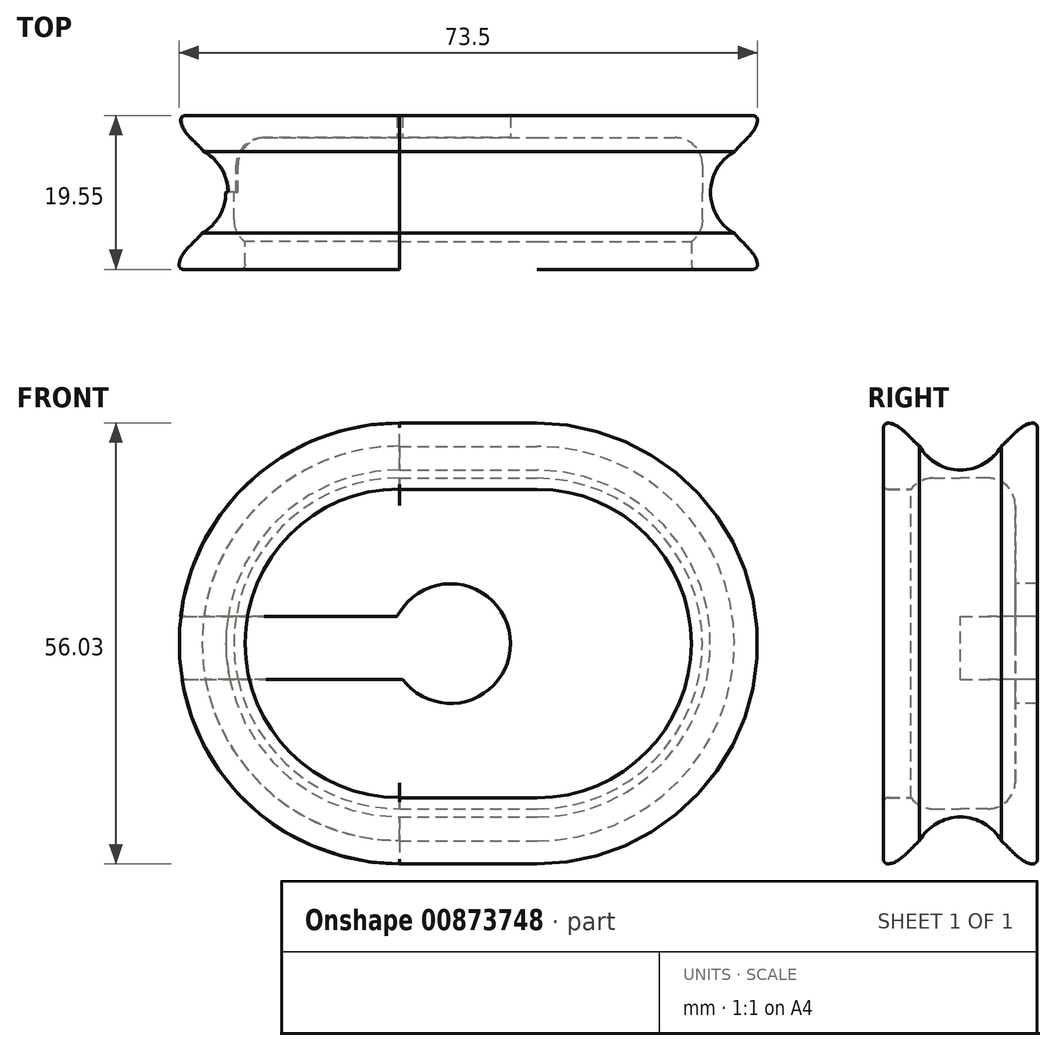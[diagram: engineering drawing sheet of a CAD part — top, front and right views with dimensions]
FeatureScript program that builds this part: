
annotation { "Feature Type Name" : "Feature", "Feature Type Description" : "" }
export const myFeature = defineFeature(function(context is Context, id is Id, definition is map)
    precondition{}
    {
        {
            var Q0;
            Q0=qCreatedBy(makeId("Top.planeOp"),FACE);
            var sketch = newSketch(context, id + "F0", { "sketchPlane" : qUnion([Q0])});
            skLineSegment(sketch, "E0", {"start": v(32.84, -14) * mm, "end": v(32.86, 13.93) * mm, "construction": true});
            skLineSegment(sketch, "E1", {"start": v(39.15, 13.93) * mm, "end": v(0, 13.93) * mm});
            skLineSegment(sketch, "E2", {"start": v(-31.68, 0) * mm, "end": v(51.3, -0.04) * mm, "construction": true});
            skLineSegment(sketch, "E3", {"start": v(26.86, 4.13) * mm, "end": v(26.83, 4.13) * mm, "construction": true});
            skFitSpline(sketch, "E4", {"points": [v(34.01, 4.12) * mm, v(40, 13.93) * mm], "startDerivative": vector(3.62, 13.63) * mm, "endDerivative": vector(-1.34, 11.55) * mm});
            skFitSpline(sketch, "E5.MirrorCS", {"points": [v(34, -4.19) * mm, v(40, -14) * mm], "startDerivative": vector(3.6, -13.63) * mm, "endDerivative": vector(-1.35, -11.55) * mm});
            skLineSegment(sketch, "E6", {"start": v(30.01, 4.92) * mm, "end": v(30.01, -0.03) * mm});
            skLineSegment(sketch, "E7", {"start": v(0, 9.93) * mm, "end": v(0, 13.93) * mm});
            skArc(sketch, "E8.filletArc", {"start": v(30.01, 4.92) * mm, "mid": v(28.55, 8.46) * mm, "end": v(25.01, 9.92) * mm});
            skArc(sketch, "E9.MirrorCS", {"start": v(30, -4.98) * mm, "mid": v(29.47, -7.22) * mm, "end": v(28, -8.99) * mm});
            skLineSegment(sketch, "E10.MirrorCS", {"start": v(30, -4.98) * mm, "end": v(30.01, -0.03) * mm});
            skLineSegment(sketch, "E11", {"start": v(28, -13.13) * mm, "end": v(28, -8.99) * mm});
            skLineSegment(sketch, "E12", {"start": v(0, 3.85) * mm, "end": v(40, 3.83) * mm, "construction": true});
            skLineSegment(sketch, "E13", {"start": v(40, 18.61) * mm, "end": v(40, -32.14) * mm, "construction": true});
            skLineSegment(sketch, "E14", {"start": v(25.01, 9.92) * mm, "end": v(0, 9.93) * mm});
            skLineSegment(sketch, "E15", {"start": v(39.14, -14) * mm, "end": v(28.85, -13.99) * mm});
            skLineSegment(sketch, "E16", {"start": v(36.5, -1.52) * mm, "end": v(36.51, 2.9) * mm, "construction": true});
            skArc(sketch, "E17", {"start": v(35.8, 7.37) * mm, "mid": v(31.48, -0.03) * mm, "end": v(35.8, -7.44) * mm});
            skArc(sketch, "E18.filletArc", {"start": v(39.14, -14) * mm, "mid": v(39.78, -13.7) * mm, "end": v(39.99, -13.02) * mm});
            skArc(sketch, "E19.filletArc", {"start": v(40, 12.95) * mm, "mid": v(39.8, 13.63) * mm, "end": v(39.15, 13.93) * mm});
            skPoint(sketch, "E20.visualSharp", {"position": v(28, -13.99) * mm});
            skArc(sketch, "E20.filletArc", {"start": v(28, -13.13) * mm, "mid": v(28.24, -13.74) * mm, "end": v(28.85, -13.99) * mm});
            skSolve(sketch);
        }
        {
            var Q0;
            Q0=qSketchRegion(id+"F0",true);
            var Q1;
            Q1=qSketchRegion(id+"F0",true);
            var Q2;
            Q2=makeQuery(id+"F0.imprint","IMPRINT",FACE,{"disambiguationData":[TD([[makeQuery(id+"F0.imprint","IMPRINT",EDGE,{"derivedFrom":sQuery(id+"F0.wireOp",EDGE,"E1")}),1.0]])]});
            var Q3;
            Q3=sQuery(id+"F0.wireOp",EDGE,"YOEqnzkB-9UwB-SSfj-woJi-8cwrd5BflBc7");
            var Q4;
            Q4=sQuery(id+"F0.wireOp",EDGE,"E7");
            revolve(context, id + "F1", {"surfaceOperationType" : NewSurfaceOperationType.NEW, "entities" : qUnion([Q0, Q1, Q2]), "axis" : qUnion([Q3, Q4]), "revolveType" : RevolveType.SYMMETRIC, "angle" : 180 * degree});
        }
        {
            var Q0;
            Q0=makeQuery(id+"F1.opRevolve","CAP_FACE",FACE,{"disambiguationData":[OSD([sQuery(id+"F0.wireOp",EDGE,"E1"),sQuery(id+"F0.wireOp",EDGE,"E4"),sQuery(id+"F0.wireOp",EDGE,"pFRlobtz-0q4r-BGyK-Zf5O-oVfqoQiTMujq"),sQuery(id+"F0.wireOp",EDGE,"0d47ac5b-4a7f-461a-a2c7-a7ca7c96fb220.MirrorCS"),sQuery(id+"F0.wireOp",EDGE,"E5.MirrorCS"),sQuery(id+"F0.wireOp",EDGE,"mUEO9S0t-vfNT-DUiq-7ehG-LlwwYBXUM1qr"),sQuery(id+"F0.wireOp",EDGE,"E6"),sQuery(id+"F0.wireOp",EDGE,"E7"),sQuery(id+"F0.wireOp",EDGE,"E8.filletArc"),sQuery(id+"F0.wireOp",EDGE,"E9.MirrorCS"),sQuery(id+"F0.wireOp",EDGE,"E10.MirrorCS"),sQuery(id+"F0.wireOp",EDGE,"DfFPZrzA-9eie-ccyR-lrFW-XJ07qiCjYuLb"),sQuery(id+"F0.wireOp",EDGE,"E11")])],"isStart":false});
            extrude(context, id + "F2", {"entities" : qUnion([Q0]), "operationType" : NewBodyOperationType.ADD, "depth" : 25 * mm, "offsetDistance" : 25 * mm});
        }
        {
            var Q0;
            Q0=makeQuery(id+"F2.opExtrude","CAP_FACE",FACE,{"disambiguationData":[OSD([sQuery(id+"F0.wireOp",EDGE,"E1"),sQuery(id+"F0.wireOp",EDGE,"E4"),sQuery(id+"F0.wireOp",EDGE,"pFRlobtz-0q4r-BGyK-Zf5O-oVfqoQiTMujq"),sQuery(id+"F0.wireOp",EDGE,"0d47ac5b-4a7f-461a-a2c7-a7ca7c96fb220.MirrorCS"),sQuery(id+"F0.wireOp",EDGE,"E5.MirrorCS"),sQuery(id+"F0.wireOp",EDGE,"mUEO9S0t-vfNT-DUiq-7ehG-LlwwYBXUM1qr"),sQuery(id+"F0.wireOp",EDGE,"E6"),sQuery(id+"F0.wireOp",EDGE,"E7"),sQuery(id+"F0.wireOp",EDGE,"E8.filletArc"),sQuery(id+"F0.wireOp",EDGE,"E9.MirrorCS"),sQuery(id+"F0.wireOp",EDGE,"E10.MirrorCS"),sQuery(id+"F0.wireOp",EDGE,"DfFPZrzA-9eie-ccyR-lrFW-XJ07qiCjYuLb"),sQuery(id+"F0.wireOp",EDGE,"E11")])],"isStart":false});
            cPlane(context, id + "F3", {"entities" : qUnion([Q0]), "cplaneType" : CPlaneType.OFFSET, "offset" : 0 * mm, "width" : 150 * mm, "height" : 150 * mm});
        }
        {
            var Q0;
            Q0=qCreatedBy(id+"F3.planeOp",FACE);
            var sketch = newSketch(context, id + "F4", { "sketchPlane" : qUnion([Q0])});
            skLineSegment(sketch, "E21", {"start": v(14, 32.88) * mm, "end": v(-13.93, 32.9) * mm, "construction": true});
            skLineSegment(sketch, "E22", {"start": v(-0.01, -31.64) * mm, "end": v(0.03, 51.34) * mm, "construction": true});
            skLineSegment(sketch, "E23", {"start": v(-4.13, 26.9) * mm, "end": v(-4.13, 26.86) * mm, "construction": true});
            skFitSpline(sketch, "E24", {"points": [v(-4.13, 34.05) * mm, v(-13.93, 40.04) * mm], "startDerivative": vector(-13.63, 3.62) * mm, "endDerivative": vector(-11.55, -1.34) * mm});
            skLineSegment(sketch, "E25", {"start": v(13.22, 0.04) * mm, "end": v(-13.1, 0.04) * mm, "construction": true});
            skFitSpline(sketch, "E26.MirrorCS", {"points": [v(4.19, 34.04) * mm, v(14, 40.03) * mm], "startDerivative": vector(13.63, 3.6) * mm, "endDerivative": vector(11.55, -1.35) * mm});
            skLineSegment(sketch, "E27", {"start": v(-9.93, 0.04) * mm, "end": v(-9.93, 17.9) * mm});
            skLineSegment(sketch, "E28", {"start": v(-4.93, 30.05) * mm, "end": v(0.03, 30.05) * mm});
            skLineSegment(sketch, "E29", {"start": v(-9.93, 0.04) * mm, "end": v(-13.93, 0.04) * mm});
            skPoint(sketch, "E30.visualSharp", {"position": v(-9.93, 22.9) * mm});
            skArc(sketch, "E30.filletArc", {"start": v(-4.93, 30.05) * mm, "mid": v(-8.46, 28.58) * mm, "end": v(-9.93, 25.05) * mm});
            skArc(sketch, "E31.MirrorCS", {"start": v(4.98, 30.04) * mm, "mid": v(7.22, 29.5) * mm, "end": v(8.99, 28.03) * mm});
            skLineSegment(sketch, "E32.MirrorCS", {"start": v(4.98, 30.04) * mm, "end": v(0.03, 30.05) * mm});
            skLineSegment(sketch, "E33", {"start": v(13.13, 28.03) * mm, "end": v(8.99, 28.03) * mm});
            skLineSegment(sketch, "E34", {"start": v(-13.93, 0.04) * mm, "end": v(-13.93, 39.18) * mm});
            skLineSegment(sketch, "E35", {"start": v(13.99, 28.88) * mm, "end": v(14, 39.18) * mm});
            skLineSegment(sketch, "E36", {"start": v(-9.93, 17.9) * mm, "end": v(-9.93, 25.05) * mm});
            skLineSegment(sketch, "E37", {"start": v(-13.93, 40.04) * mm, "end": v(14, 40.03) * mm, "construction": true});
            skArc(sketch, "E38", {"start": v(7.42, 35.82) * mm, "mid": v(0, 31.52) * mm, "end": v(-7.4, 35.85) * mm});
            skPoint(sketch, "E39.visualSharp", {"position": v(13.99, 28.03) * mm});
            skArc(sketch, "E39.filletArc", {"start": v(13.13, 28.03) * mm, "mid": v(13.74, 28.28) * mm, "end": v(13.99, 28.88) * mm});
            skArc(sketch, "E40.filletArc", {"start": v(-12.95, 40.03) * mm, "mid": v(-13.63, 39.83) * mm, "end": v(-13.93, 39.18) * mm});
            skArc(sketch, "E41.filletArc", {"start": v(14, 39.18) * mm, "mid": v(13.7, 39.82) * mm, "end": v(13.02, 40.02) * mm});
            skSolve(sketch);
        }
        {
            var Q0;
            Q0=makeQuery(id+"F4.imprint","IMPRINT",FACE,{"disambiguationData":[TD([[makeQuery(id+"F4.imprint","IMPRINT",EDGE,{"derivedFrom":sQuery(id+"F4.wireOp",EDGE,"E24")}),1.0]])]});
            var Q1;
            Q1=sQuery(id+"F4.wireOp",EDGE,"E25");
            revolve(context, id + "F5", {"operationType" : NewBodyOperationType.ADD, "surfaceOperationType" : NewSurfaceOperationType.NEW, "entities" : qUnion([Q0]), "axis" : qUnion([Q1]), "revolveType" : RevolveType.ONE_DIRECTION, "oppositeDirection" : true, "angle" : 180 * degree});
        }
        {
            var Q0;
            Q0=makeQuery(id+"F1.opRevolve","SWEPT_BODY",BODY,{"disambiguationData":[OSD([sQuery(id+"F0.wireOp",EDGE,"E1"),sQuery(id+"F0.wireOp",EDGE,"E4"),sQuery(id+"F0.wireOp",EDGE,"pFRlobtz-0q4r-BGyK-Zf5O-oVfqoQiTMujq"),sQuery(id+"F0.wireOp",EDGE,"0d47ac5b-4a7f-461a-a2c7-a7ca7c96fb220.MirrorCS"),sQuery(id+"F0.wireOp",EDGE,"E5.MirrorCS"),sQuery(id+"F0.wireOp",EDGE,"mUEO9S0t-vfNT-DUiq-7ehG-LlwwYBXUM1qr"),sQuery(id+"F0.wireOp",EDGE,"E6"),sQuery(id+"F0.wireOp",EDGE,"E7"),sQuery(id+"F0.wireOp",EDGE,"E8.filletArc"),sQuery(id+"F0.wireOp",EDGE,"E9.MirrorCS"),sQuery(id+"F0.wireOp",EDGE,"E10.MirrorCS"),sQuery(id+"F0.wireOp",EDGE,"DfFPZrzA-9eie-ccyR-lrFW-XJ07qiCjYuLb"),sQuery(id+"F0.wireOp",EDGE,"E11")])]});
            var Q1;
            Q1=qCreatedBy(makeId("Origin.pointOp"),VERTEX);
            transform(context, id + "F6", {"entities" : qUnion([Q0]), "transformType" : TransformType.SCALE_UNIFORMLY, "scale" : .7, "scalePoint" : qUnion([Q1]), "makeCopy" : false});
        }
        {
            var Q0;
            Q0=qCreatedBy(makeId("Front.planeOp"),FACE);
            var sketch = newSketch(context, id + "F7", { "sketchPlane" : qUnion([Q0])});
            skLineSegment(sketch, "E42", {"start": v(29.26, 0) * mm, "end": v(-58.04, 0) * mm, "construction": true});
            skLineSegment(sketch, "E43", {"start": v(-10.99, -28.68) * mm, "end": v(-10.99, 40.74) * mm, "construction": true});
            skLineSegment(sketch, "E44.bottom", {"start": v(-17.8, 3.43) * mm, "end": v(-45.99, 3.43) * mm});
            skLineSegment(sketch, "E44.top", {"start": v(-17.09, -4.57) * mm, "end": v(-45.99, -4.57) * mm});
            skPoint(sketch, "E45", {"position": v(-10.99, 0) * mm});
            skArc(sketch, "E46", {"start": v(-17.8, 3.43) * mm, "mid": v(-3.4, 0.67) * mm, "end": v(-17.09, -4.57) * mm});
            skLineSegment(sketch, "E47", {"start": v(-71.37, 3.43) * mm, "end": v(-71.37, -4.57) * mm});
            skLineSegment(sketch, "E48", {"start": v(-71.37, -4.57) * mm, "end": v(-45.99, -4.57) * mm});
            skLineSegment(sketch, "E49", {"start": v(-45.99, 3.43) * mm, "end": v(-71.37, 3.43) * mm});
            skSolve(sketch);
        }
        {
            var Q0;
            Q0=makeQuery(id+"F7.imprint","IMPRINT",FACE,{"disambiguationData":[TD([[makeQuery(id+"F7.imprint","IMPRINT",EDGE,{"derivedFrom":sQuery(id+"F7.wireOp",EDGE,"E44.bottom")}),1.0]])]});
            extrude(context, id + "F8", {"entities" : qUnion([Q0]), "operationType" : NewBodyOperationType.REMOVE, "oppositeDirection" : true, "depth" : 15 * mm, "offsetDistance" : 25 * mm});
        }
    });
